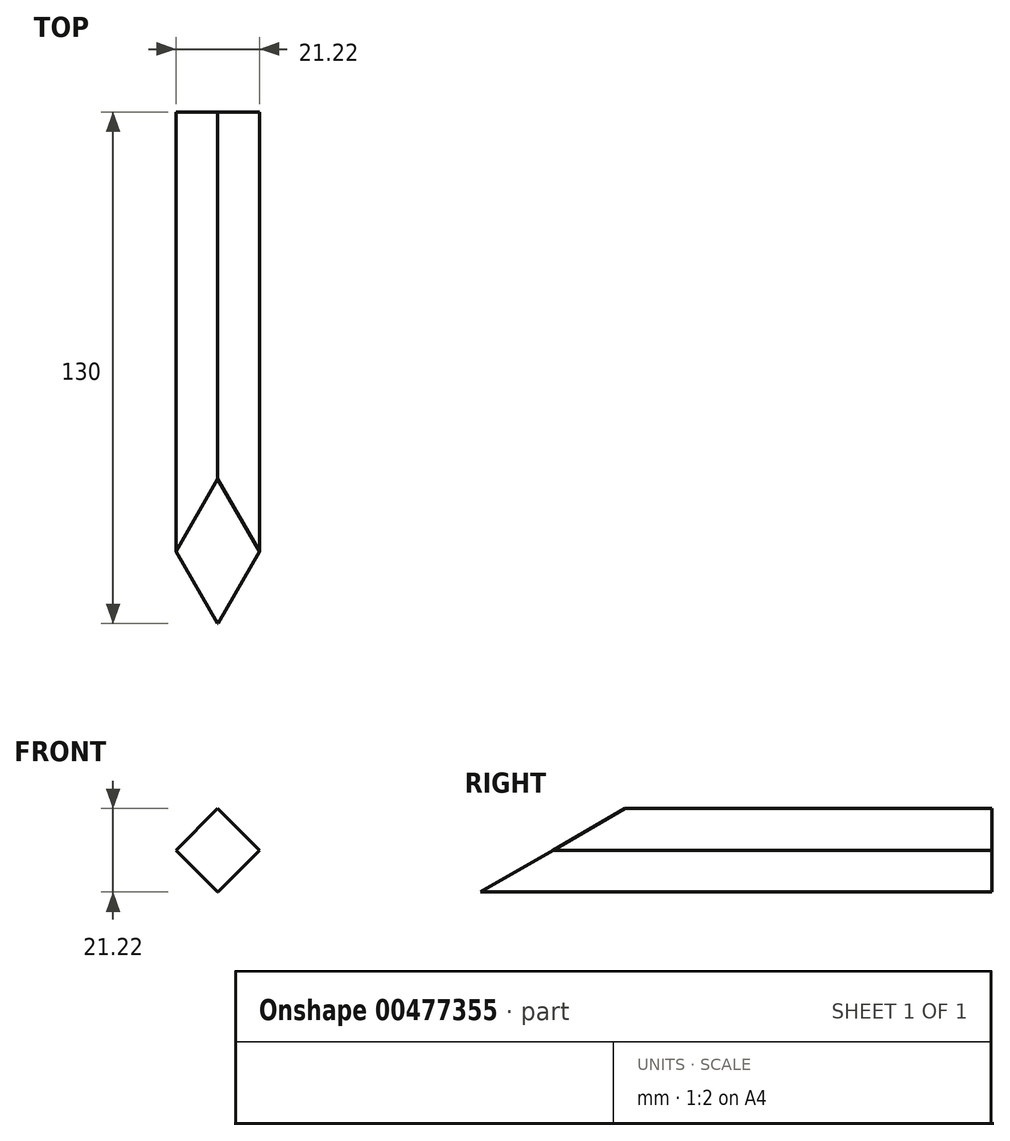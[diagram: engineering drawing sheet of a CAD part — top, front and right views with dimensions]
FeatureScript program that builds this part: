
annotation { "Feature Type Name" : "Feature", "Feature Type Description" : "" }
export const myFeature = defineFeature(function(context is Context, id is Id, definition is map)
    precondition{}
    {
        {
            var Q0;
            Q0=qCreatedBy(makeId("Front.planeOp"),FACE);
            var sketch = newSketch(context, id + "F0", { "sketchPlane" : qUnion([Q0])});
            skLineSegment(sketch, "E0", {"start": v(-10.6, 0) * mm, "end": v(0, 10.6) * mm});
            skLineSegment(sketch, "E1", {"start": v(0, 10.6) * mm, "end": v(10.6, 0) * mm});
            skLineSegment(sketch, "E2", {"start": v(10.6, 0) * mm, "end": v(0, -10.6) * mm});
            skLineSegment(sketch, "E3", {"start": v(0, -10.6) * mm, "end": v(-10.6, 0) * mm});
            skSolve(sketch);
        }
        {
            var Q0;
            Q0 = qSketchRegion(id + "F0", true);
            extrude(context, id + "F1", {"entities" : qUnion([Q0]), "depth" : 130 * mm});
        }
        {
            var Q0;
            Q0=qCreatedBy(makeId("Right.planeOp"),FACE);
            var sketch = newSketch(context, id + "F2", { "sketchPlane" : qUnion([Q0])});
            skLineSegment(sketch, "E4", {"start": v(-130, -10.6) * mm, "end": v(-92.9, 10.82) * mm});
            skLineSegment(sketch, "E5", {"start": v(-92.9, 10.82) * mm, "end": v(-130, 10.82) * mm});
            skLineSegment(sketch, "E6", {"start": v(-130, 10.82) * mm, "end": v(-130, -10.6) * mm});
            skSolve(sketch);
        }
        {
            var Q0;
            Q0 = qSketchRegion(id + "F2", true);
            extrude(context, id + "F3", {"entities" : qUnion([Q0]), "operationType" : NewBodyOperationType.REMOVE, "endBound" : BoundingType.SYMMETRIC, "oppositeDirection" : true, "depth" : 25 * mm});
        }
    });
